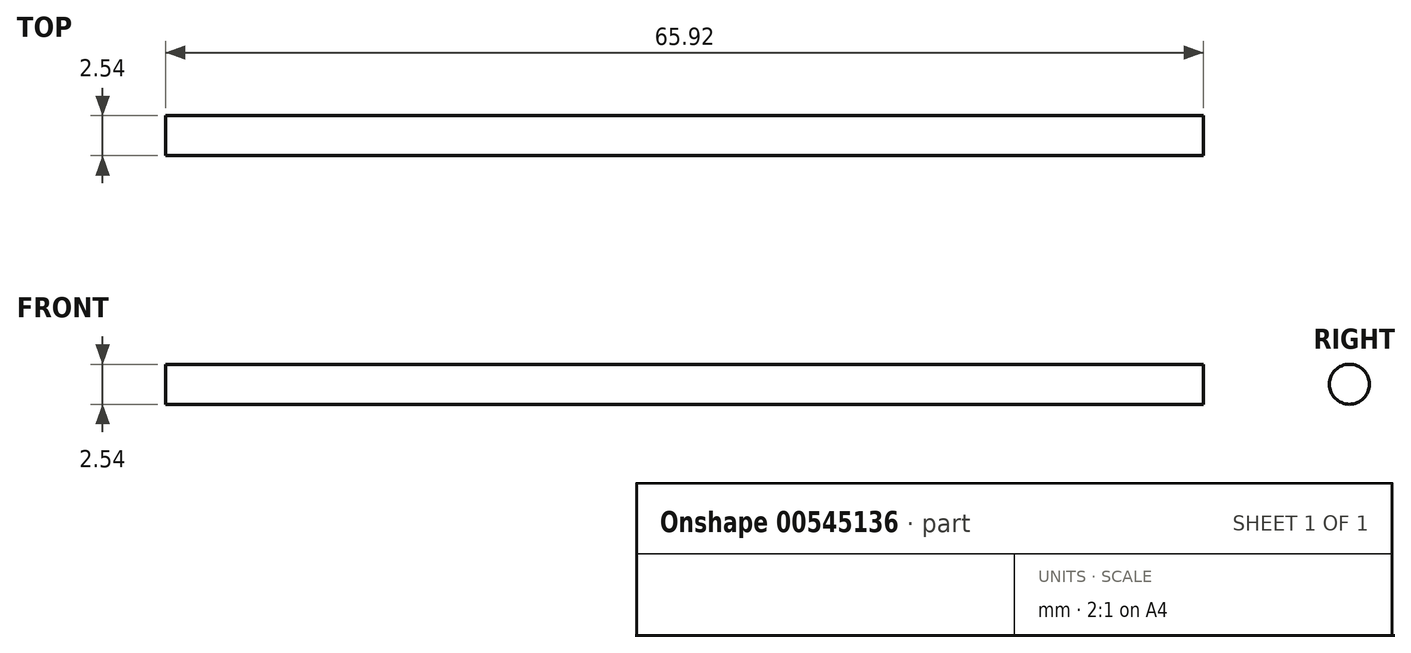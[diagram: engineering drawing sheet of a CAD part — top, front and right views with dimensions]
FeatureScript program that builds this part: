
annotation { "Feature Type Name" : "Feature", "Feature Type Description" : "" }
export const myFeature = defineFeature(function(context is Context, id is Id, definition is map)
    precondition{}
    {
        {
            var Q0;
            Q0=qCreatedBy(makeId("Right.planeOp"),FACE);
            var sketch = newSketch(context, id + "F0", { "sketchPlane" : qUnion([Q0])});
            skCircle(sketch, "E0", {"center": v(0, 0) * mm, "radius": 1.27 * mm});
            skSolve(sketch);
        }
        {
            var Q0;
            Q0 = qSketchRegion(id + "F0", true);
            extrude(context, id + "F1", {"entities" : qUnion([Q0]), "endBound" : BoundingType.SYMMETRIC, "depth" : 65.9 * mm, "offsetDistance" : 25.4 * mm});
        }
    });
